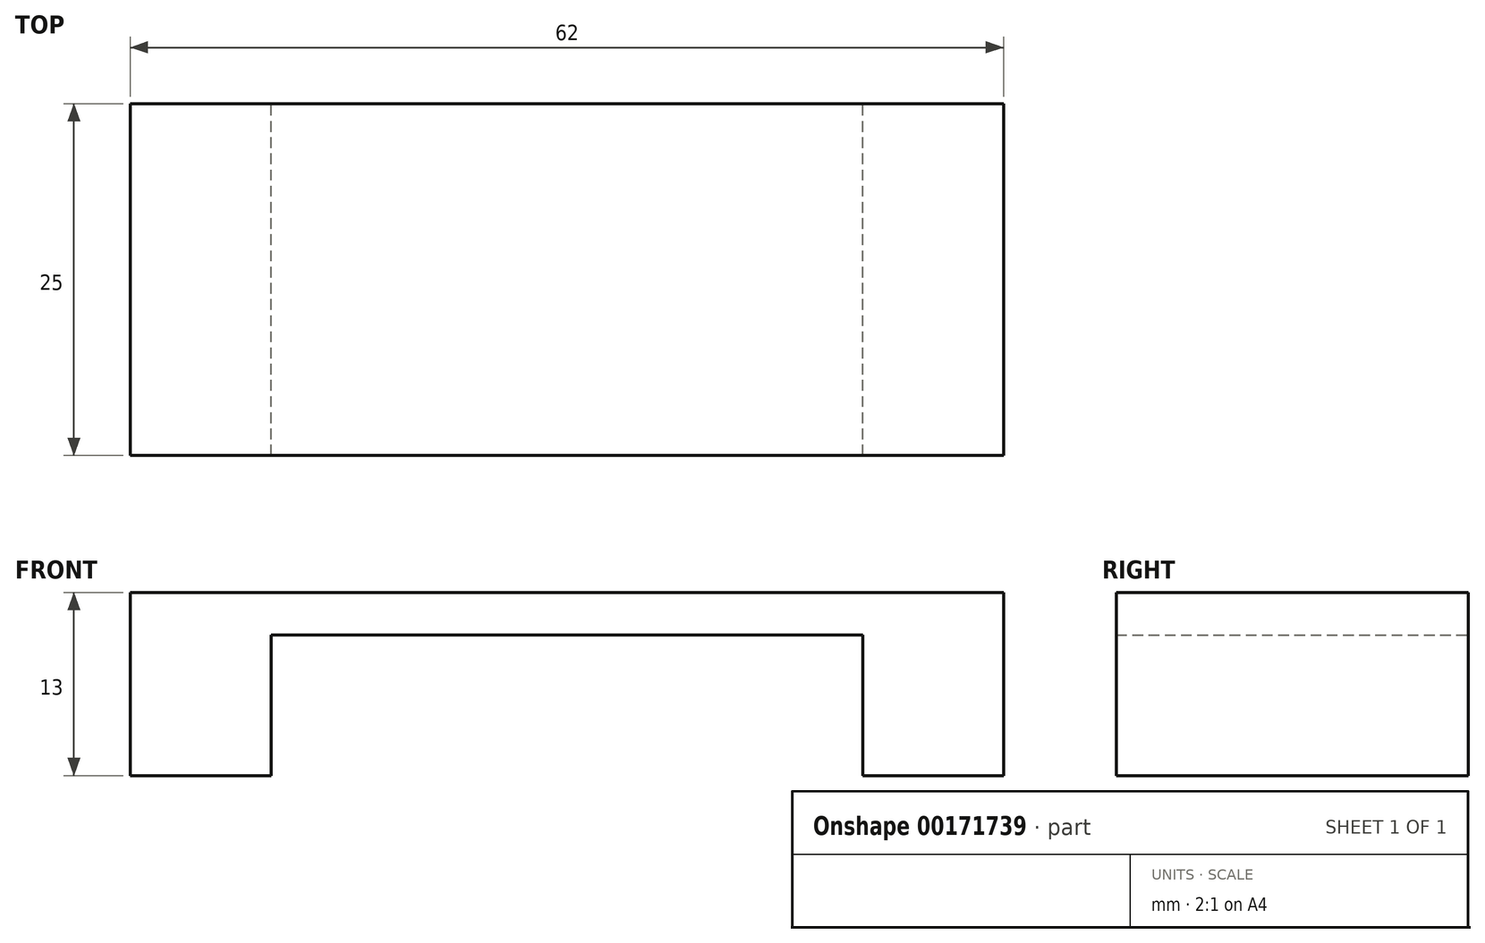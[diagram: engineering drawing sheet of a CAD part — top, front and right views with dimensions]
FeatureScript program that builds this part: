
annotation { "Feature Type Name" : "Feature", "Feature Type Description" : "" }
export const myFeature = defineFeature(function(context is Context, id is Id, definition is map)
    precondition{}
    {
        {
            var Q0;
            Q0=qCreatedBy(makeId("Front.planeOp"),FACE);
            var sketch = newSketch(context, id + "F0", { "sketchPlane" : qUnion([Q0])});
            skLineSegment(sketch, "E0", {"start": v(0, 0) * mm, "end": v(62, 0) * mm});
            skLineSegment(sketch, "E1", {"start": v(62, 0) * mm, "end": v(62, -13) * mm});
            skLineSegment(sketch, "E2", {"start": v(62, -13) * mm, "end": v(52, -13) * mm});
            skLineSegment(sketch, "E3", {"start": v(52, -13) * mm, "end": v(52, -3) * mm});
            skLineSegment(sketch, "E4", {"start": v(52, -3) * mm, "end": v(10, -3) * mm});
            skLineSegment(sketch, "E5", {"start": v(10, -3) * mm, "end": v(10, -13) * mm});
            skLineSegment(sketch, "E6", {"start": v(10, -13) * mm, "end": v(0, -13) * mm});
            skLineSegment(sketch, "E7", {"start": v(0, -13) * mm, "end": v(0, 0) * mm});
            skSolve(sketch);
        }
        {
            var Q0;
            Q0 = qSketchRegion(id + "F0", true);
            extrude(context, id + "F1", {"entities" : qUnion([Q0]), "depth" : 25 * mm});
        }
    });
